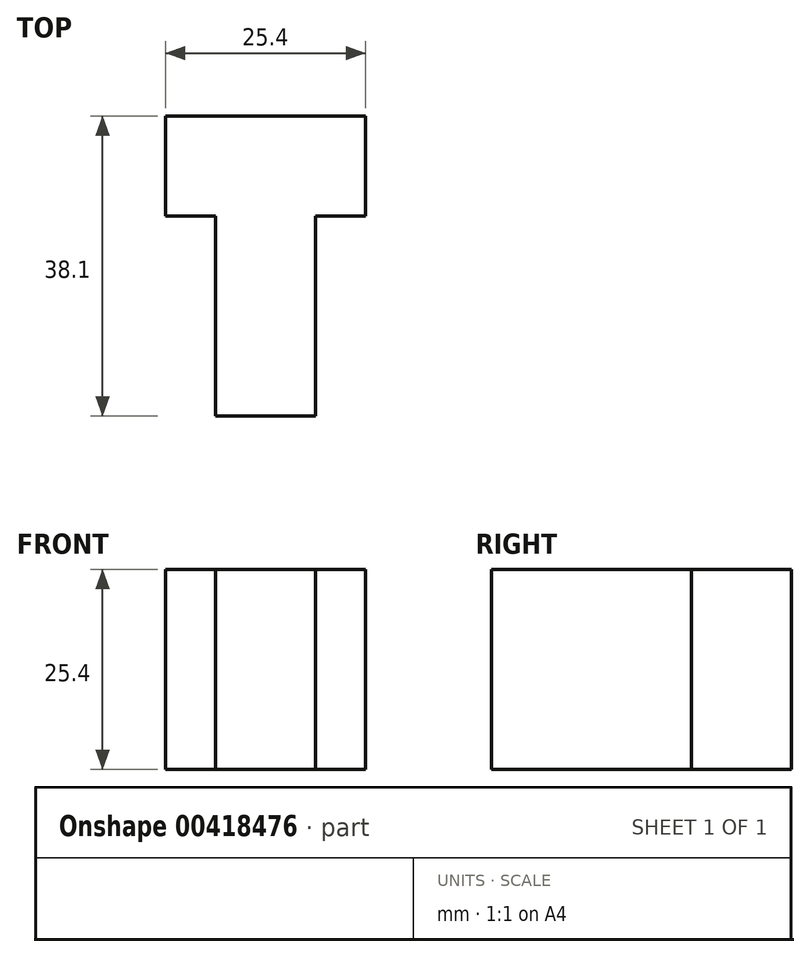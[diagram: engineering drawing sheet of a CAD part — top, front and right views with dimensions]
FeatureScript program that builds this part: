
annotation { "Feature Type Name" : "Feature", "Feature Type Description" : "" }
export const myFeature = defineFeature(function(context is Context, id is Id, definition is map)
    precondition{}
    {
        {
            var Q0;
            Q0=qCreatedBy(makeId("Top.planeOp"),FACE);
            var sketch = newSketch(context, id + "F0", { "sketchPlane" : qUnion([Q0])});
            skLineSegment(sketch, "E0", {"start": v(0, 0) * mm, "end": v(4.64, 0) * mm});
            skLineSegment(sketch, "E1", {"start": v(4.64, 0) * mm, "end": v(4.64, 25.4) * mm});
            skLineSegment(sketch, "E2", {"start": v(4.64, 25.4) * mm, "end": v(11, 25.4) * mm});
            skLineSegment(sketch, "E3", {"start": v(11, 25.4) * mm, "end": v(11, 38.1) * mm});
            skLineSegment(sketch, "E4", {"start": v(11, 38.1) * mm, "end": v(-14.4, 38.1) * mm});
            skLineSegment(sketch, "E5", {"start": v(-14.4, 38.1) * mm, "end": v(-14.4, 25.4) * mm});
            skLineSegment(sketch, "E6", {"start": v(-14.4, 25.4) * mm, "end": v(-8.06, 25.4) * mm});
            skLineSegment(sketch, "E7", {"start": v(-8.06, 25.4) * mm, "end": v(-8.06, 0) * mm});
            skLineSegment(sketch, "E8", {"start": v(-8.06, 0) * mm, "end": v(4.64, 0) * mm});
            skSolve(sketch);
        }
        {
            var Q0;
            Q0 = qSketchRegion(id + "F0", true);
            extrude(context, id + "F1", {"entities" : qUnion([Q0]), "depth" : 25.4 * mm});
        }
    });
